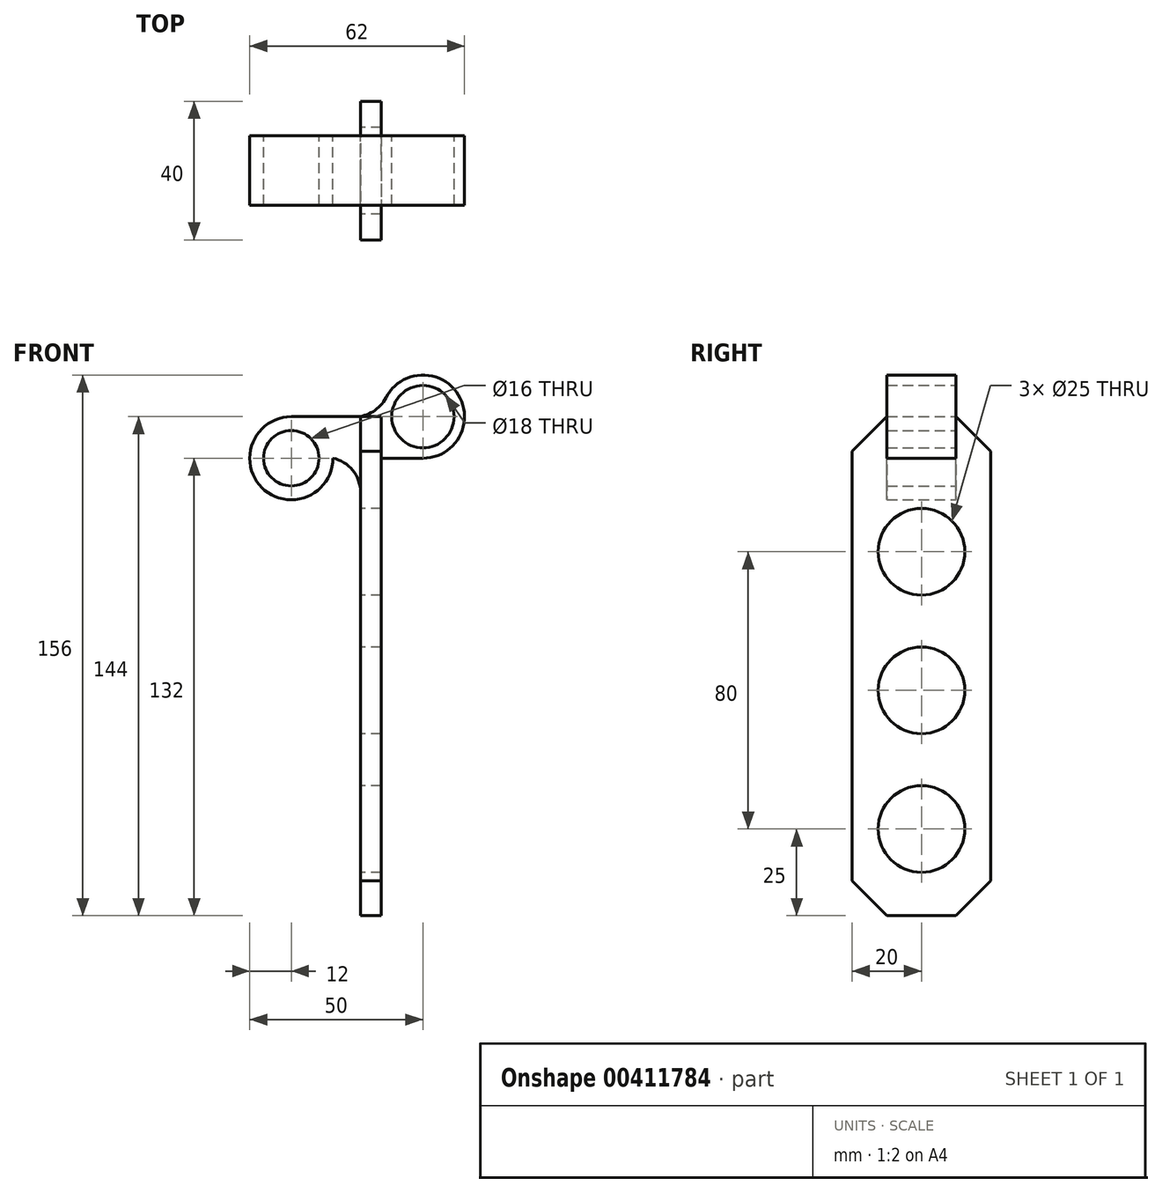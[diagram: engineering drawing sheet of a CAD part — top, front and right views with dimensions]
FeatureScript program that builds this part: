
annotation { "Feature Type Name" : "Feature", "Feature Type Description" : "" }
export const myFeature = defineFeature(function(context is Context, id is Id, definition is map)
    precondition{}
    {
        {
            var Q0;
            Q0=qCreatedBy(makeId("Front.planeOp"),FACE);
            var sketch = newSketch(context, id + "F0", { "sketchPlane" : qUnion([Q0])});
            skCircle(sketch, "E0", {"center": v(0, 0) * mm, "radius": 8 * mm});
            skCircle(sketch, "E1", {"center": v(38, 12) * mm, "radius": 9 * mm});
            skCircle(sketch, "E2", {"center": v(0, 0) * mm, "radius": 12 * mm});
            skCircle(sketch, "E3", {"center": v(38, 12) * mm, "radius": 12 * mm});
            skLineSegment(sketch, "E4", {"start": v(0, 12) * mm, "end": v(26, 12) * mm});
            skLineSegment(sketch, "E5", {"start": v(38, 0) * mm, "end": v(12, 0) * mm});
            skSolve(sketch);
        }
        {
            var Q0;
            Q0=qSketchRegion(id+"F0",true);
            extrude(context, id + "F1", {"entities" : qUnion([Q0]), "depth" : 20 * mm});
        }
        {
            var Q0;
            Q0=makeQuery(id+"F1.opExtrude","CAP_FACE",FACE,{"disambiguationData":[OSD([sQuery(id+"F0.wireOp",EDGE,"E0"),sQuery(id+"F0.wireOp",EDGE,"E1"),sQuery(id+"F0.wireOp",EDGE,"E2"),sQuery(id+"F0.wireOp",EDGE,"E3"),sQuery(id+"F0.wireOp",EDGE,"E4"),sQuery(id+"F0.wireOp",EDGE,"E5")])],"isStart":false});
            var sketch = newSketch(context, id + "F2", { "sketchPlane" : qUnion([Q0])});
            skLineSegment(sketch, "E6.bottom", {"start": v(26, 12) * mm, "end": v(20, 12) * mm});
            skLineSegment(sketch, "E6.top", {"start": v(26, -132) * mm, "end": v(20, -132) * mm});
            skLineSegment(sketch, "E6.left", {"start": v(26, 12) * mm, "end": v(26, -132) * mm});
            skLineSegment(sketch, "E6.right", {"start": v(20, 12) * mm, "end": v(20, -132) * mm});
            skSolve(sketch);
        }
        {
            var Q0;
            Q0=qSketchRegion(id+"F2",true);
            extrude(context, id + "F3", {"entities" : qUnion([Q0]), "operationType" : NewBodyOperationType.ADD, "depth" : 10 * mm, "hasSecondDirection" : true, "secondDirectionOppositeDirection" : true, "secondDirectionDepth" : 30 * mm});
        }
        {
            var Q0;
            Q0=makeQuery(id+"F3.opExtrude","CAP_EDGE",EDGE,{"disambiguationData":[OSD([sQuery(id+"F2.wireOp",EDGE,"E6.bottom")])],"isStart":false});
            var Q1;
            Q1=makeQuery(id+"F3.opExtrude","CAP_EDGE",EDGE,{"disambiguationData":[OSD([sQuery(id+"F2.wireOp",EDGE,"E6.bottom")])],"isStart":true});
            var Q2;
            Q2=makeQuery(id+"F3.opExtrude","CAP_EDGE",EDGE,{"disambiguationData":[OSD([sQuery(id+"F2.wireOp",EDGE,"E6.top")])],"isStart":false});
            var Q3;
            Q3=makeQuery(id+"F3.opExtrude","CAP_EDGE",EDGE,{"disambiguationData":[OSD([sQuery(id+"F2.wireOp",EDGE,"E6.top")])],"isStart":true});
            chamfer(context, id + "F4", {"entities" : qUnion([Q0, Q1, Q2, Q3]), "width" : 10 * mm, "tangentPropagation" : true});
        }
        {
            var Q0;
            Q0=makeQuery(id+"F1.opExtrude","SWEPT_EDGE",EDGE,{"disambiguationData":[OSD([sQuery(id+"F0.wireOp",EDGE,"E3"),sQuery(id+"F0.wireOp",EDGE,"E4")])]});
            var Q1;
            Q1=makeQuery(id+"F3.boolean.opBoolean","INTERSECT",EDGE,{"derivedFrom":[makeQuery(id+"F1.opExtrude","SWEPT_FACE",FACE,{"disambiguationData":[OSD([sQuery(id+"F0.wireOp",EDGE,"E5")])]}),makeQuery(id+"F3.opExtrude","SWEPT_FACE",FACE,{"disambiguationData":[OSD([sQuery(id+"F2.wireOp",EDGE,"E6.right")])]})]});
            fillet(context, id + "F5", {"entities" : qUnion([Q0, Q1]), "radius" : 10 * mm, "tangentPropagation" : true, "allowEdgeOverflow" : false});
        }
        {
            var Q0;
            Q0=makeQuery(id+"F3.opExtrude","SWEPT_FACE",FACE,{"disambiguationData":[OSD([sQuery(id+"F2.wireOp",EDGE,"E6.right")])]});
            var sketch = newSketch(context, id + "F6", { "sketchPlane" : qUnion([Q0])});
            skCircle(sketch, "E7", {"center": v(10, -107) * mm, "radius": 12.5 * mm});
            skPoint(sketch, "E7.centerSnap0", {"position": v(10, -132) * mm});
            skCircle(sketch, "E8", {"center": v(10, -67) * mm, "radius": 12.5 * mm});
            skCircle(sketch, "E9", {"center": v(10, -27) * mm, "radius": 12.5 * mm});
            skSolve(sketch);
        }
        {
            var Q0;
            Q0=qSketchRegion(id+"F6",true);
            var Q1;
            Q1=makeQuery(id+"F3.opExtrude","SWEPT_FACE",FACE,{"disambiguationData":[OSD([sQuery(id+"F2.wireOp",EDGE,"E6.left")])]});
            extrude(context, id + "F7", {"entities" : qUnion([Q0]), "operationType" : NewBodyOperationType.REMOVE, "endBound" : BoundingType.UP_TO_SURFACE, "oppositeDirection" : true, "endBoundEntityFace" : qUnion([Q1]), "depth" : 25 * mm});
        }
    });
